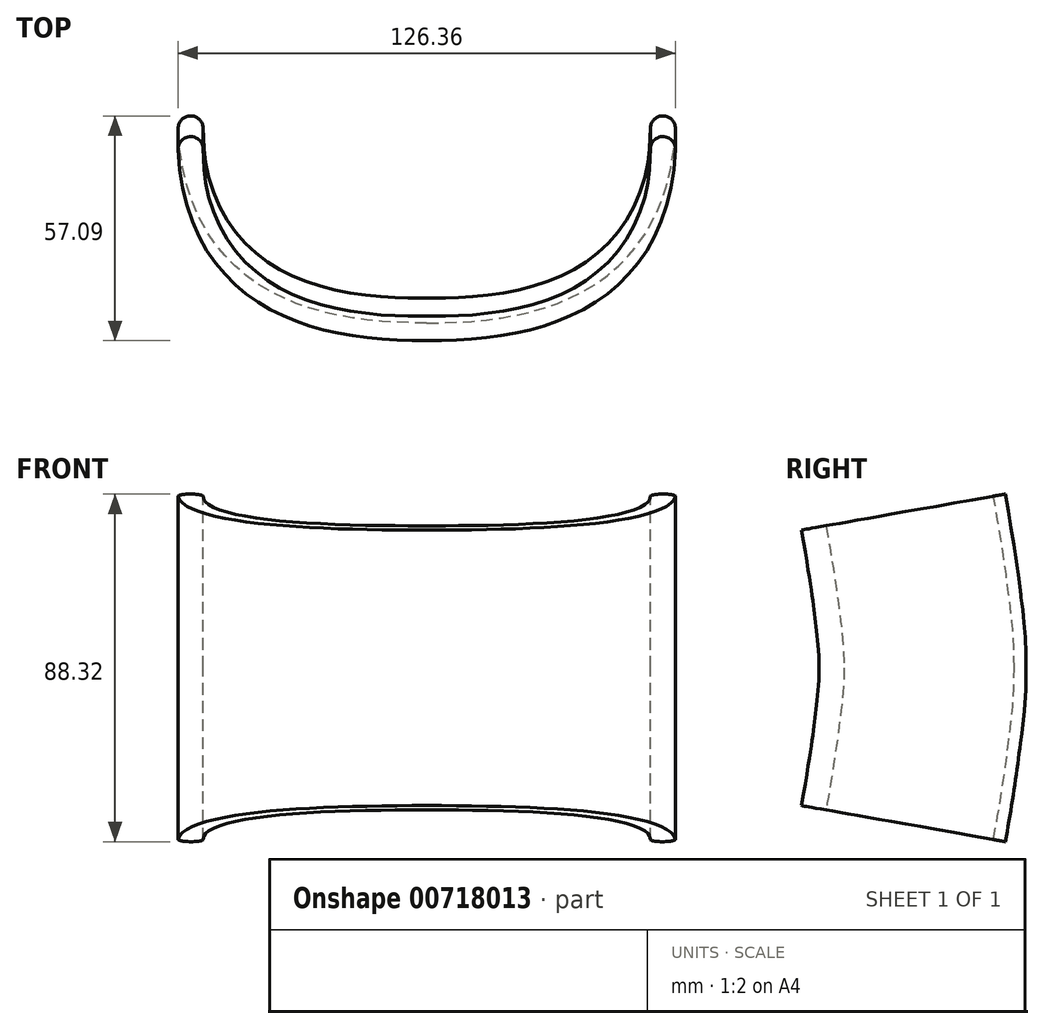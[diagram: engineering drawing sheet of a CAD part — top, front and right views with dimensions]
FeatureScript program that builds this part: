
annotation { "Feature Type Name" : "Feature", "Feature Type Description" : "" }
export const myFeature = defineFeature(function(context is Context, id is Id, definition is map)
    precondition{}
    {
        {
            var Q0;
            Q0=qCreatedBy(makeId("Top.planeOp"),FACE);
            var sketch = newSketch(context, id + "F0", { "sketchPlane" : qUnion([Q0])});
            skFitSpline(sketch, "E0", {"points": [v(0, 0) * mm, v(40.1, 8.2) * mm, v(63.17, 49.3) * mm], "startDerivative": vector(86.83, 0) * mm, "endDerivative": vector(5.72, 122.93) * mm});
            skLineSegment(sketch, "E1", {"start": v(0, 0) * mm, "end": v(0, 35.79) * mm, "construction": true});
            skFitSpline(sketch, "E2.MirrorCS", {"points": [v(0, 0) * mm, v(-40.1, 8.2) * mm, v(-63.17, 49.3) * mm], "startDerivative": vector(-86.83, 0) * mm, "endDerivative": vector(-5.72, 122.93) * mm});
            skFitSpline(sketch, "E3.0", {"points": [v(0, 6.35) * mm, v(-3.5, 6.35) * mm, v(-10.47, 6.56) * mm, v(-20.57, 7.8) * mm, v(-29.94, 10.25) * mm, v(-38.29, 14.1) * mm, v(-45.44, 19.6) * mm, v(-51.17, 26.94) * mm, v(-55.27, 36.58) * mm, v(-56.6, 44.9) * mm, v(-56.83, 49.59) * mm]});
            skFitSpline(sketch, "E3.1", {"points": [v(0, 6.35) * mm, v(3.5, 6.35) * mm, v(10.47, 6.56) * mm, v(20.57, 7.8) * mm, v(29.94, 10.25) * mm, v(38.29, 14.1) * mm, v(45.44, 19.6) * mm, v(51.17, 26.94) * mm, v(55.27, 36.58) * mm, v(56.6, 44.9) * mm, v(56.83, 49.59) * mm]});
            skArc(sketch, "E4", {"start": v(-63.17, 49.3) * mm, "mid": v(-60.15, 52.61) * mm, "end": v(-56.83, 49.59) * mm});
            skArc(sketch, "E5", {"start": v(56.83, 49.59) * mm, "mid": v(60.15, 52.61) * mm, "end": v(63.17, 49.3) * mm});
            skSolve(sketch);
        }
        {
            var Q0;
            Q0=qCreatedBy(makeId("Right.planeOp"),FACE);
            var sketch = newSketch(context, id + "F1", { "sketchPlane" : qUnion([Q0])});
            skLineSegment(sketch, "E6", {"start": v(0, 0) * mm, "end": v(-16.37, 0) * mm, "construction": true});
            skFitSpline(sketch, "E7", {"points": [v(-4.47, 35) * mm, v(-1, 12.41) * mm, v(0, 0) * mm], "startDerivative": vector(12.57, -71.05) * mm, "endDerivative": vector(0, -37.25) * mm});
            skFitSpline(sketch, "E8.MirrorCS", {"points": [v(-4.47, -35) * mm, v(-1, -12.41) * mm, v(0, 0) * mm], "startDerivative": vector(12.57, 71.05) * mm, "endDerivative": vector(0, 37.25) * mm});
            skSolve(sketch);
        }
        {
            var Q0;
            Q0=makeQuery(id+"F0.imprint","IMPRINT",FACE,{"disambiguationData":[TD([[makeQuery(id+"F0.imprint","IMPRINT",EDGE,{"derivedFrom":sQuery(id+"F0.wireOp",EDGE,"E0")}),1.0]])]});
            var Q1;
            Q1=sQuery(id+"F1.wireOp",EDGE,"E7");
            var Q2;
            Q2=sQuery(id+"F1.wireOp",EDGE,"E8.MirrorCS");
            sweep(context, id + "F2", {"profiles" : qUnion([Q0]), "path" : qUnion([Q1, Q2])});
        }
    });
